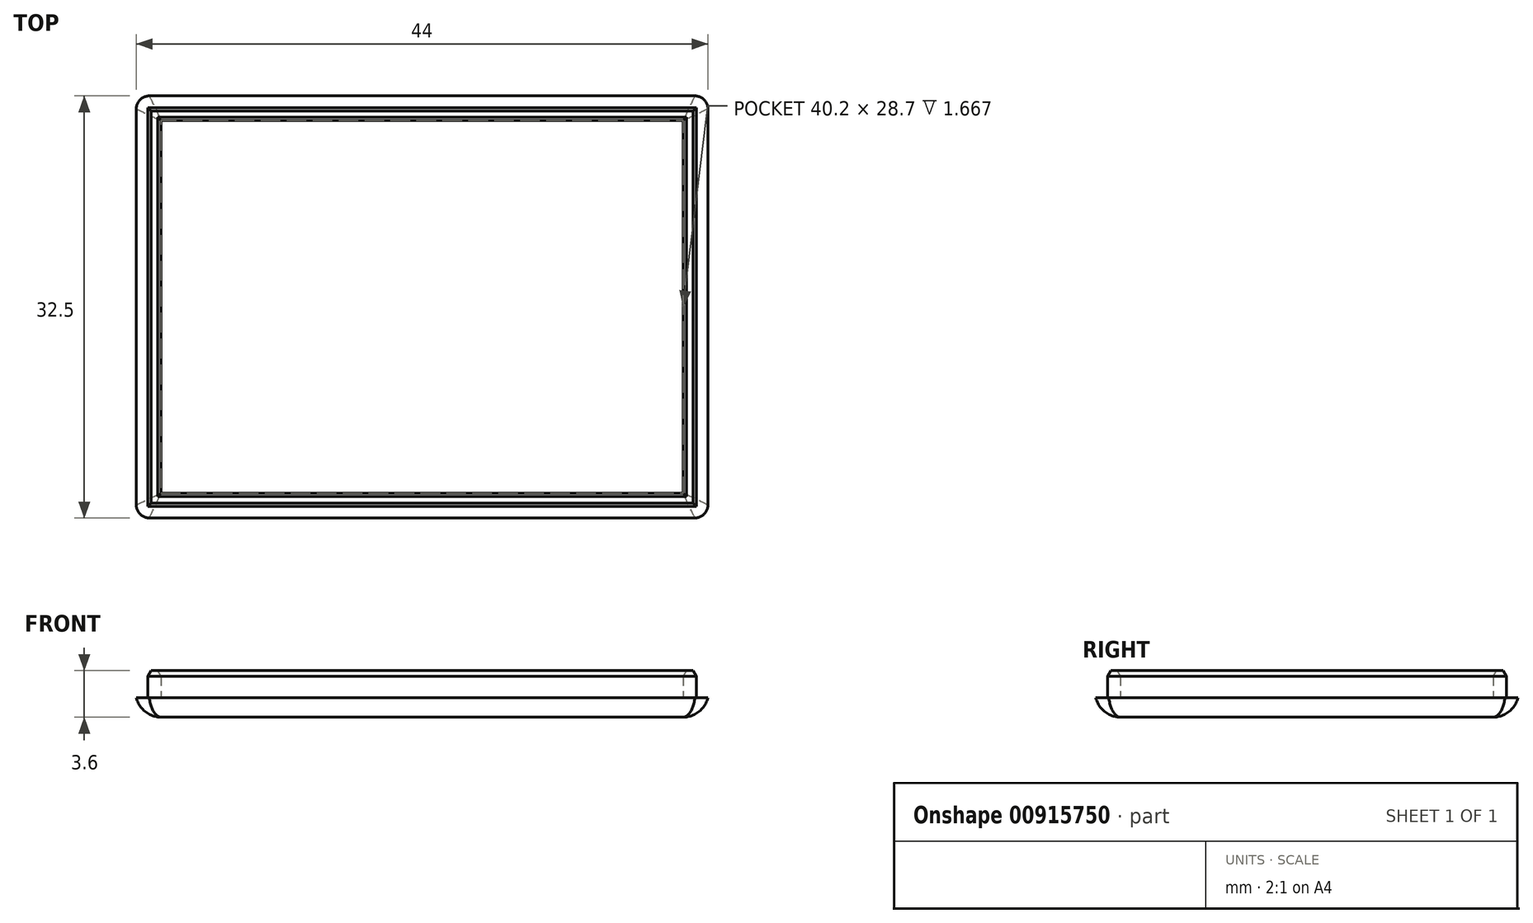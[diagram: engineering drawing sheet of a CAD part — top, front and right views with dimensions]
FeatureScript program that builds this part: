
annotation { "Feature Type Name" : "Feature", "Feature Type Description" : "" }
export const myFeature = defineFeature(function(context is Context, id is Id, definition is map)
    precondition{}
    {
        {
            var Q0;
            Q0=qCreatedBy(makeId("Top.planeOp"),FACE);
            var sketch = newSketch(context, id + "F0", { "sketchPlane" : qUnion([Q0])});
            skLineSegment(sketch, "E0.bottom", {"start": v(0, 0) * mm, "end": v(44, 0) * mm});
            skLineSegment(sketch, "E0.top", {"start": v(0, 32.5) * mm, "end": v(44, 32.5) * mm});
            skLineSegment(sketch, "E0.left", {"start": v(0, 0) * mm, "end": v(0, 32.5) * mm});
            skLineSegment(sketch, "E0.right", {"start": v(44, 0) * mm, "end": v(44, 32.5) * mm});
            skSolve(sketch);
        }
        {
            var Q0;
            Q0=makeQuery(id+"F0.imprint","IMPRINT",FACE,{"disambiguationData":[TD([[makeQuery(id+"F0.imprint","IMPRINT",EDGE,{"derivedFrom":sQuery(id+"F0.wireOp",EDGE,"E0.bottom")}),1.0]])]});
            extrude(context, id + "F1", {"entities" : qUnion([Q0]), "depth" : 1.5 * mm, "offsetDistance" : 25 * mm});
        }
        {
            var Q0;
            Q0=makeQuery(id+"F1.opExtrude","CAP_FACE",FACE,{"disambiguationData":[OSD([sQuery(id+"F0.wireOp",EDGE,"E0.bottom"),sQuery(id+"F0.wireOp",EDGE,"E0.top"),sQuery(id+"F0.wireOp",EDGE,"E0.left"),sQuery(id+"F0.wireOp",EDGE,"E0.right")])],"isStart":false});
            var sketch = newSketch(context, id + "F2", { "sketchPlane" : qUnion([Q0])});
            skLineSegment(sketch, "E1.bottom", {"start": v(0.9, 31.6) * mm, "end": v(43.1, 31.6) * mm});
            skLineSegment(sketch, "E1.top", {"start": v(0.9, 0.9) * mm, "end": v(43.1, 0.9) * mm});
            skLineSegment(sketch, "E1.left", {"start": v(0.9, 31.6) * mm, "end": v(0.9, 0.9) * mm});
            skLineSegment(sketch, "E1.right", {"start": v(43.1, 31.6) * mm, "end": v(43.1, 0.9) * mm});
            skLineSegment(sketch, "E2.bottom", {"start": v(1.9, 30.6) * mm, "end": v(42.1, 30.6) * mm});
            skLineSegment(sketch, "E2.top", {"start": v(1.9, 1.9) * mm, "end": v(42.1, 1.9) * mm});
            skLineSegment(sketch, "E2.left", {"start": v(1.9, 30.6) * mm, "end": v(1.9, 1.9) * mm});
            skLineSegment(sketch, "E2.right", {"start": v(42.1, 30.6) * mm, "end": v(42.1, 1.9) * mm});
            skSolve(sketch);
        }
        {
            var Q0;
            Q0=makeQuery(id+"F2.imprint","IMPRINT",FACE,{"disambiguationData":[TD([[makeQuery(id+"F2.imprint","IMPRINT",EDGE,{"derivedFrom":sQuery(id+"F2.wireOp",EDGE,"E1.bottom")}),-1.0]])]});
            extrude(context, id + "F3", {"entities" : qUnion([Q0]), "operationType" : NewBodyOperationType.ADD, "depth" : 2.1 * mm, "offsetDistance" : 25 * mm});
        }
        {
            var Q0;
            Q0=makeQuery(id+"F3.opExtrude","CAP_EDGE",EDGE,{"disambiguationData":[OSD([sQuery(id+"F2.wireOp",EDGE,"E1.bottom")])],"isStart":false});
            var Q1;
            Q1=makeQuery(id+"F3.opExtrude","CAP_EDGE",EDGE,{"disambiguationData":[OSD([sQuery(id+"F2.wireOp",EDGE,"E1.right")])],"isStart":false});
            var Q2;
            Q2=makeQuery(id+"F3.opExtrude","CAP_EDGE",EDGE,{"disambiguationData":[OSD([sQuery(id+"F2.wireOp",EDGE,"E1.top")])],"isStart":false});
            var Q3;
            Q3=makeQuery(id+"F3.opExtrude","CAP_EDGE",EDGE,{"disambiguationData":[OSD([sQuery(id+"F2.wireOp",EDGE,"E1.left")])],"isStart":false});
            var Q4;
            Q4=makeQuery(id+"F3.opExtrude","CAP_EDGE",EDGE,{"disambiguationData":[OSD([sQuery(id+"F2.wireOp",EDGE,"E2.bottom")])],"isStart":false});
            var Q5;
            Q5=makeQuery(id+"F3.opExtrude","CAP_EDGE",EDGE,{"disambiguationData":[OSD([sQuery(id+"F2.wireOp",EDGE,"E2.right")])],"isStart":false});
            var Q6;
            Q6=makeQuery(id+"F3.opExtrude","CAP_EDGE",EDGE,{"disambiguationData":[OSD([sQuery(id+"F2.wireOp",EDGE,"E2.top")])],"isStart":false});
            var Q7;
            Q7=makeQuery(id+"F3.opExtrude","CAP_EDGE",EDGE,{"disambiguationData":[OSD([sQuery(id+"F2.wireOp",EDGE,"E2.left")])],"isStart":false});
            chamfer(context, id + "F4", {"entities" : qUnion([Q0, Q1, Q2, Q3, Q4, Q5, Q6, Q7]), "chamferType" : ChamferType.OFFSET_ANGLE, "width" : .25 * mm, "oppositeDirection" : true, "angle" : 60 * degree, "tangentPropagation" : true});
        }
        {
            var Q0;
            Q0=makeQuery(id+"F1.opExtrude","SWEPT_EDGE",EDGE,{"disambiguationData":[OSD([sQuery(id+"F0.wireOp",EDGE,"E0.bottom"),sQuery(id+"F0.wireOp",EDGE,"E0.left")])]});
            var Q1;
            Q1=makeQuery(id+"F1.opExtrude","SWEPT_EDGE",EDGE,{"disambiguationData":[OSD([sQuery(id+"F0.wireOp",EDGE,"E0.top"),sQuery(id+"F0.wireOp",EDGE,"E0.left")])]});
            var Q2;
            Q2=makeQuery(id+"F1.opExtrude","SWEPT_EDGE",EDGE,{"disambiguationData":[OSD([sQuery(id+"F0.wireOp",EDGE,"E0.bottom"),sQuery(id+"F0.wireOp",EDGE,"E0.right")])]});
            var Q3;
            Q3=makeQuery(id+"F1.opExtrude","SWEPT_EDGE",EDGE,{"disambiguationData":[OSD([sQuery(id+"F0.wireOp",EDGE,"E0.top"),sQuery(id+"F0.wireOp",EDGE,"E0.right")])]});
            fillet(context, id + "F5", {"entities" : qUnion([Q0, Q1, Q2, Q3]), "radius" : 1 * mm, "tangentPropagation" : true, "allowEdgeOverflow" : false});
        }
        {
            var Q0;
            Q0=makeQuery(id+"F1.opExtrude","CAP_EDGE",EDGE,{"disambiguationData":[OSD([sQuery(id+"F0.wireOp",EDGE,"E0.left")])],"isStart":true});
            fillet(context, id + "F6", {"entities" : qUnion([Q0]), "radius" : 2 * mm, "tangentPropagation" : true, "allowEdgeOverflow" : false});
        }
    });
